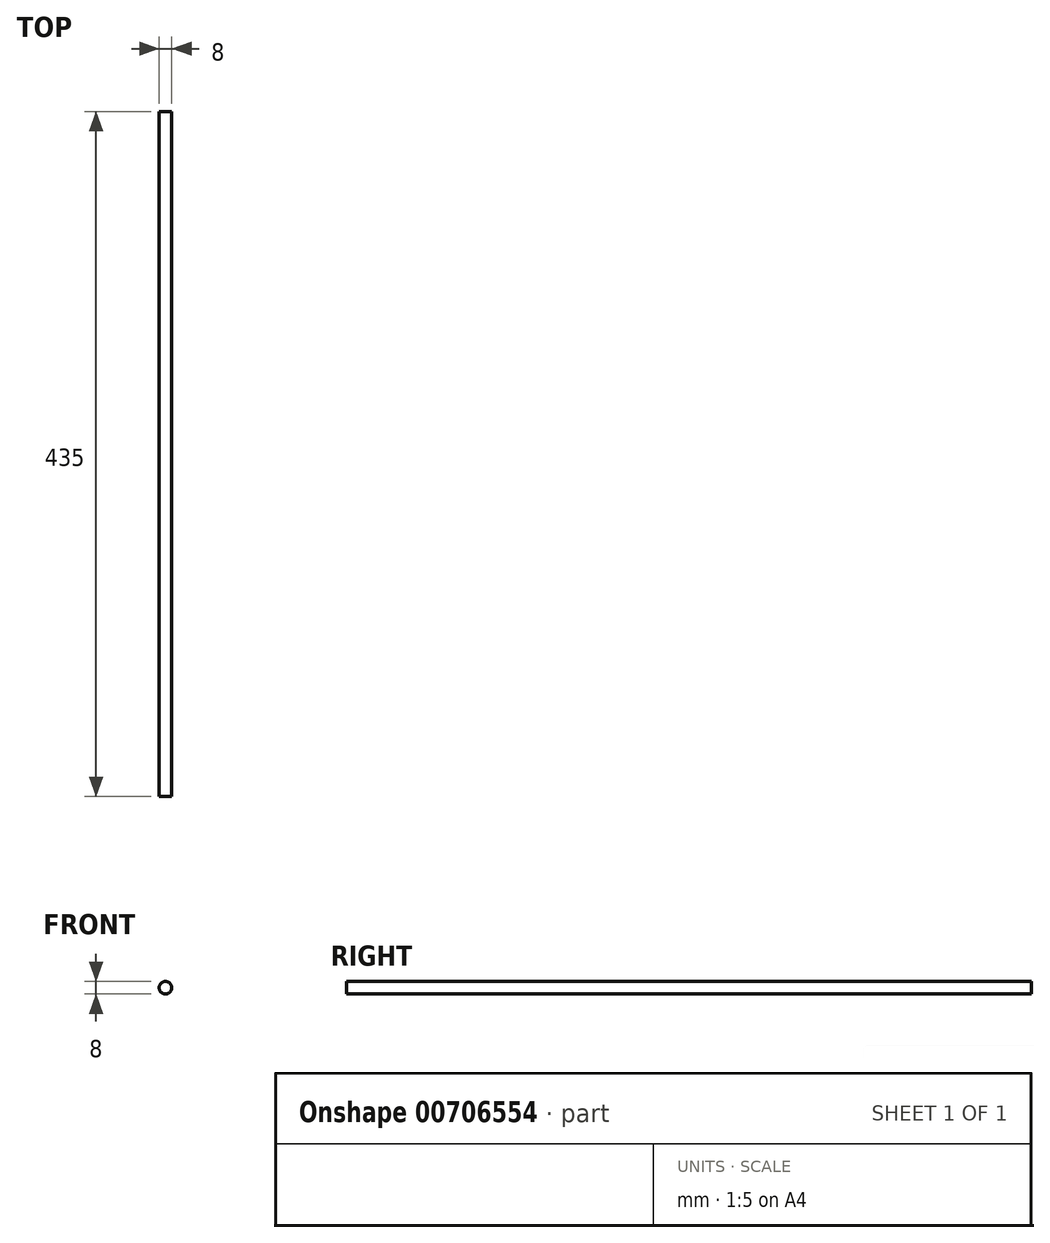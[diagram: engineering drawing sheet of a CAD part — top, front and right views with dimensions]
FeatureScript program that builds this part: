
annotation { "Feature Type Name" : "Feature", "Feature Type Description" : "" }
export const myFeature = defineFeature(function(context is Context, id is Id, definition is map)
    precondition{}
    {
        {
            var Q0;
            Q0=qCreatedBy(makeId("Front.planeOp"),FACE);
            var sketch = newSketch(context, id + "F0", { "sketchPlane" : qUnion([Q0])});
            skCircle(sketch, "E0", {"center": v(0, 0) * mm, "radius": 4 * mm});
            skSolve(sketch);
        }
        {
            var Q0;
            Q0=qSketchRegion(id+"F0",true);
            extrude(context, id + "F1", {"entities" : qUnion([Q0]), "depth" : 435 * mm, "offsetDistance" : 25.4 * mm});
        }
    });
